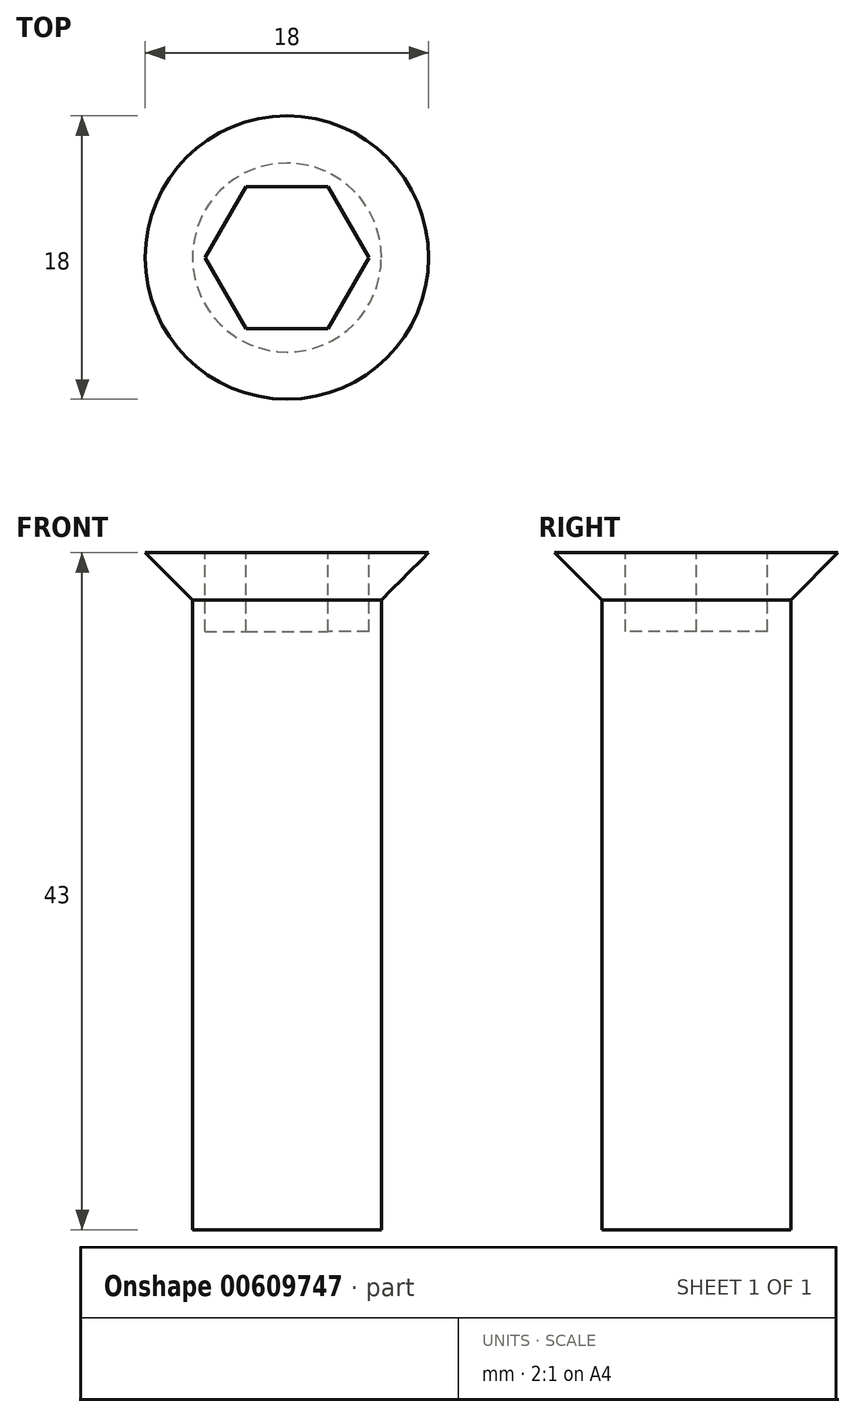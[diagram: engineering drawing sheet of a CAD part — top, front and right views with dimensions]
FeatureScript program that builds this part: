
annotation { "Feature Type Name" : "Feature", "Feature Type Description" : "" }
export const myFeature = defineFeature(function(context is Context, id is Id, definition is map)
    precondition{}
    {
        {
            var Q0;
            Q0=qCreatedBy(makeId("Top.planeOp"),FACE);
            var sketch = newSketch(context, id + "F0", { "sketchPlane" : qUnion([Q0])});
            skCircle(sketch, "E0", {"center": v(0, 0) * mm, "radius": 6 * mm});
            skSolve(sketch);
        }
        {
            var Q0;
            Q0=makeQuery(id+"F0.imprint","IMPRINT",FACE,{"disambiguationData":[TD([[makeQuery(id+"F0.imprint","IMPRINT",EDGE,{"derivedFrom":sQuery(id+"F0.wireOp",EDGE,"E0")}),1.0]])]});
            extrude(context, id + "F1", {"entities" : qUnion([Q0]), "depth" : 3 * mm, "offsetDistance" : 25 * mm, "hasDraft" : true, "draftAngle" : 45 * degree});
        }
        {
            var Q0;
            Q0 = qSketchRegion(id + "F0", true);
            extrude(context, id + "F2", {"entities" : qUnion([Q0]), "operationType" : NewBodyOperationType.ADD, "oppositeDirection" : true, "depth" : 40 * mm, "offsetDistance" : 25 * mm});
        }
        {
            var Q0;
            Q0=makeQuery(id+"F1.opExtrude","CAP_FACE",FACE,{"disambiguationData":[OSD([sQuery(id+"F0.wireOp",EDGE,"E0")])],"isStart":false});
            var sketch = newSketch(context, id + "F3", { "sketchPlane" : qUnion([Q0])});
            skCircle(sketch, "E1.cCircle", {"center": v(0, 0) * mm, "radius": 4.51 * mm, "construction": true});
            skLineSegment(sketch, "E1.0", {"start": v(5.21, 0) * mm, "end": v(2.6, -4.51) * mm});
            skLineSegment(sketch, "E1.1", {"start": v(2.6, -4.51) * mm, "end": v(-2.6, -4.51) * mm});
            skLineSegment(sketch, "E1.2", {"start": v(-2.6, -4.51) * mm, "end": v(-5.21, 0) * mm});
            skLineSegment(sketch, "E1.3", {"start": v(-5.21, 0) * mm, "end": v(-2.6, 4.51) * mm});
            skLineSegment(sketch, "E1.4", {"start": v(-2.6, 4.51) * mm, "end": v(2.6, 4.51) * mm});
            skLineSegment(sketch, "E1.5", {"start": v(2.6, 4.51) * mm, "end": v(5.21, 0) * mm});
            skPoint(sketch, "E1.0.midPoint", {"position": v(3.9, -2.26) * mm});
            skSolve(sketch);
        }
        {
            var Q0;
            Q0 = qSketchRegion(id + "F3", true);
            extrude(context, id + "F4", {"entities" : qUnion([Q0]), "operationType" : NewBodyOperationType.REMOVE, "oppositeDirection" : true, "depth" : 5 * mm, "offsetDistance" : 25 * mm});
        }
    });
